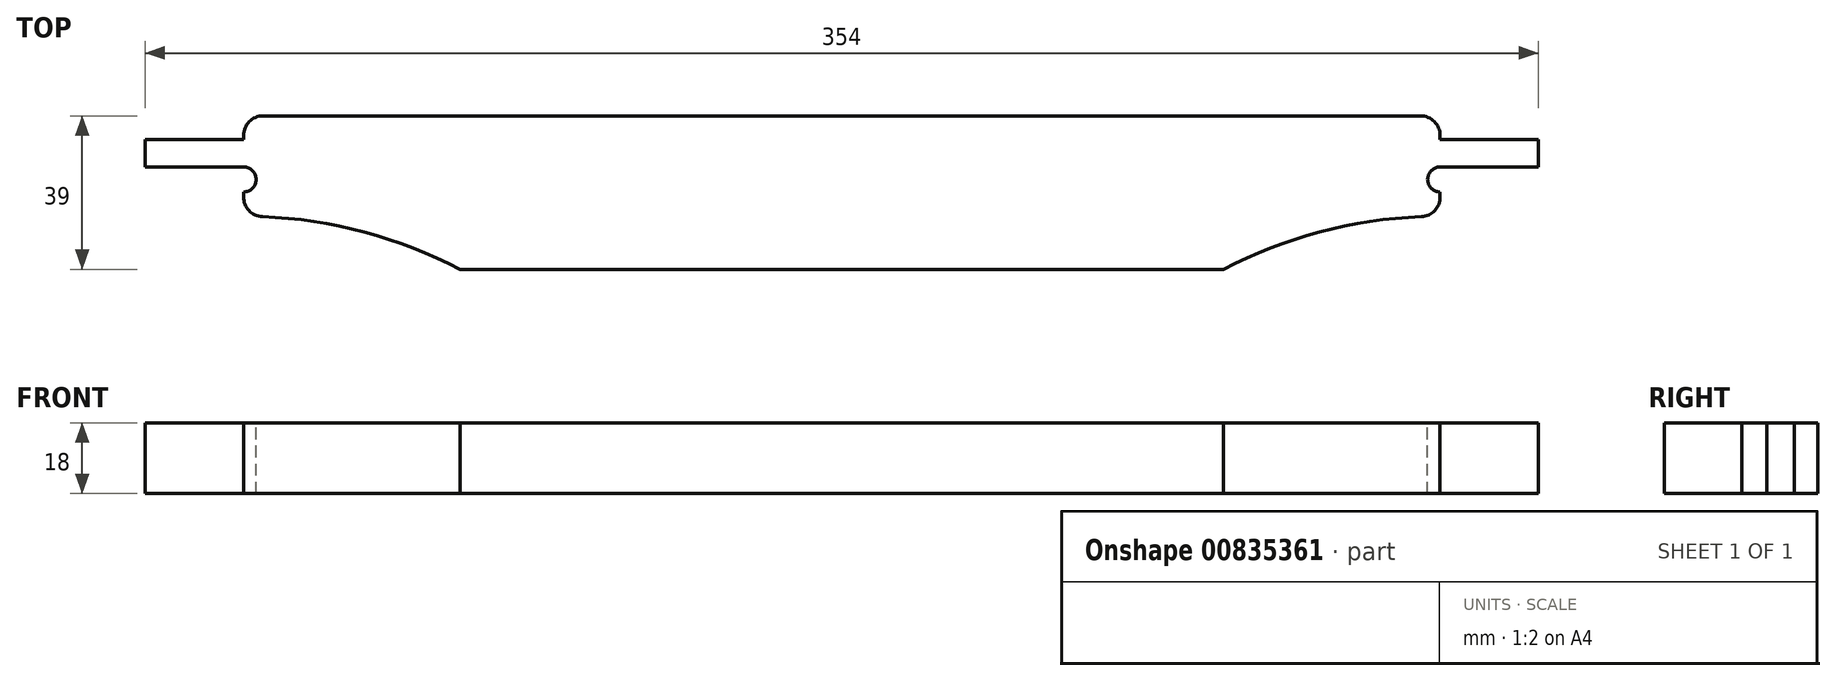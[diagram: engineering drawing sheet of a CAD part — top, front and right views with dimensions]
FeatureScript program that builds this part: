
annotation { "Feature Type Name" : "Feature", "Feature Type Description" : "" }
export const myFeature = defineFeature(function(context is Context, id is Id, definition is map)
    precondition{}
    {
        {
            var Q0;
            Q0=qCreatedBy(makeId("Top.planeOp"),FACE);
            var sketch = newSketch(context, id + "F0", { "sketchPlane" : qUnion([Q0])});
            skLineSegment(sketch, "E0", {"start": v(0, 49.79) * mm, "end": v(0, -51.17) * mm, "construction": true});
            skLineSegment(sketch, "E1", {"start": v(-177, 0) * mm, "end": v(-177, 7) * mm});
            skLineSegment(sketch, "E2", {"start": v(-177, 7) * mm, "end": v(-152, 7) * mm});
            skLineSegment(sketch, "E3", {"start": v(-177, 0) * mm, "end": v(-152, 0) * mm});
            skLineSegment(sketch, "E4", {"start": v(-97, -26) * mm, "end": v(0, -26) * mm});
            skLineSegment(sketch, "E5.MirrorCS", {"start": v(177, 7) * mm, "end": v(152, 7) * mm});
            skLineSegment(sketch, "E6.MirrorCS", {"start": v(177, 0) * mm, "end": v(177, 7) * mm});
            skLineSegment(sketch, "E7.MirrorCS", {"start": v(177, 0) * mm, "end": v(152, 0) * mm});
            skLineSegment(sketch, "E8.MirrorCS", {"start": v(97, -26) * mm, "end": v(0, -26) * mm});
            skLineSegment(sketch, "E9", {"start": v(-152, 0) * mm, "end": v(-152, -12.5) * mm});
            skLineSegment(sketch, "E10", {"start": v(-152, -12.5) * mm, "end": v(-90.35, -12.5) * mm, "construction": true});
            skArc(sketch, "E11", {"start": v(-97, -26) * mm, "mid": v(-123.68, -15.92) * mm, "end": v(-152, -12.5) * mm});
            skLineSegment(sketch, "E12.MirrorCS", {"start": v(152, 0) * mm, "end": v(152, -12.5) * mm});
            skArc(sketch, "E13.MirrorCS", {"start": v(97, -26) * mm, "mid": v(123.68, -15.92) * mm, "end": v(152, -12.5) * mm});
            skLineSegment(sketch, "E14", {"start": v(-152, 0) * mm, "end": v(-152, 7) * mm, "construction": true});
            skLineSegment(sketch, "E15", {"start": v(-152, 7) * mm, "end": v(-152, 13) * mm});
            skLineSegment(sketch, "E16", {"start": v(-152, 13) * mm, "end": v(0, 13) * mm});
            skPoint(sketch, "E17.orphan", {"position": v(0, 7) * mm});
            skLineSegment(sketch, "E18.MirrorCS", {"start": v(152, 13) * mm, "end": v(0, 13) * mm});
            skLineSegment(sketch, "E19.MirrorCS", {"start": v(152, 7) * mm, "end": v(152, 13) * mm});
            skLineSegment(sketch, "E20", {"start": v(-164.5, 7) * mm, "end": v(-164.5, 0) * mm, "construction": true});
            skLineSegment(sketch, "E21", {"start": v(164.5, 7) * mm, "end": v(164.5, 0) * mm, "construction": true});
            skSolve(sketch);
        }
        {
            var Q0;
            Q0 = qSketchRegion(id + "F0", true);
            extrude(context, id + "F1", {"entities" : qUnion([Q0]), "depth" : 18 * mm, "offsetDistance" : 25 * mm});
        }
        {
            var Q0;
            Q0=makeQuery(id+"F1.opExtrude","SWEPT_EDGE",EDGE,{"disambiguationData":[OSD([sQuery(id+"F0.wireOp",EDGE,"E9"),sQuery(id+"F0.wireOp",EDGE,"E11")])]});
            var Q1;
            Q1=makeQuery(id+"F1.opExtrude","SWEPT_EDGE",EDGE,{"disambiguationData":[OSD([sQuery(id+"F0.wireOp",EDGE,"E12.MirrorCS"),sQuery(id+"F0.wireOp",EDGE,"E13.MirrorCS")])]});
            fillet(context, id + "F2", {"entities" : qUnion([Q0, Q1]), "radius" : 5 * mm, "tangentPropagation" : true, "allowEdgeOverflow" : false});
        }
        {
            var Q0;
            Q0=makeQuery(id+"F1.opExtrude","CAP_FACE",FACE,{"disambiguationData":[OSD([sQuery(id+"F0.wireOp",EDGE,"E1"),sQuery(id+"F0.wireOp",EDGE,"E2"),sQuery(id+"F0.wireOp",EDGE,"E3"),sQuery(id+"F0.wireOp",EDGE,"E4"),sQuery(id+"F0.wireOp",EDGE,"E5.MirrorCS"),sQuery(id+"F0.wireOp",EDGE,"E6.MirrorCS"),sQuery(id+"F0.wireOp",EDGE,"E8.MirrorCS"),sQuery(id+"F0.wireOp",EDGE,"E9"),sQuery(id+"F0.wireOp",EDGE,"E11"),sQuery(id+"F0.wireOp",EDGE,"E7.MirrorCS"),sQuery(id+"F0.wireOp",EDGE,"E12.MirrorCS"),sQuery(id+"F0.wireOp",EDGE,"E13.MirrorCS")])],"isStart":false});
            var sketch = newSketch(context, id + "F3", { "sketchPlane" : qUnion([Q0])});
            skArc(sketch, "E22", {"start": v(-152, -6.36) * mm, "mid": v(-148.82, -3.18) * mm, "end": v(-152, 0) * mm});
            skArc(sketch, "E23", {"start": v(152, 0) * mm, "mid": v(148.82, -3.17) * mm, "end": v(152, -6.35) * mm});
            skSolve(sketch);
        }
        {
            var Q0;
            Q0 = qSketchRegion(id + "F3", true);
            var Q1;
            {var subQ0=sQuery(id+"F3.wireOp",EDGE,"E23");Q1=makeQuery(id+"F3.imprint","IMPRINT",FACE,{"disambiguationData":[TD([[makeQuery(id+"F3.imprint","IMPRINT",EDGE,{"derivedFrom":subQ0}),1.0]])]});}
            var Q2;
            {var subQ0=sQuery(id+"F3.wireOp",EDGE,"E22");Q2=makeQuery(id+"F3.imprint","IMPRINT",FACE,{"disambiguationData":[TD([[makeQuery(id+"F3.imprint","IMPRINT",EDGE,{"derivedFrom":subQ0}),1.0]])]});}
            extrude(context, id + "F4", {"entities" : qUnion([Q0, Q1, Q2]), "operationType" : NewBodyOperationType.REMOVE, "endBound" : BoundingType.THROUGH_ALL, "oppositeDirection" : true, "depth" : 25 * mm, "offsetDistance" : 25 * mm});
        }
        {
            var Q0;
            Q0=makeQuery(id+"F1.opExtrude","SWEPT_EDGE",EDGE,{"disambiguationData":[OSD([sQuery(id+"F0.wireOp",EDGE,"E15"),sQuery(id+"F0.wireOp",EDGE,"E16")])]});
            var Q1;
            Q1=makeQuery(id+"F1.opExtrude","SWEPT_EDGE",EDGE,{"disambiguationData":[OSD([sQuery(id+"F0.wireOp",EDGE,"E18.MirrorCS"),sQuery(id+"F0.wireOp",EDGE,"E19.MirrorCS")])]});
            fillet(context, id + "F5", {"entities" : qUnion([Q0, Q1]), "radius" : 5 * mm, "tangentPropagation" : true, "allowEdgeOverflow" : false});
        }
    });
